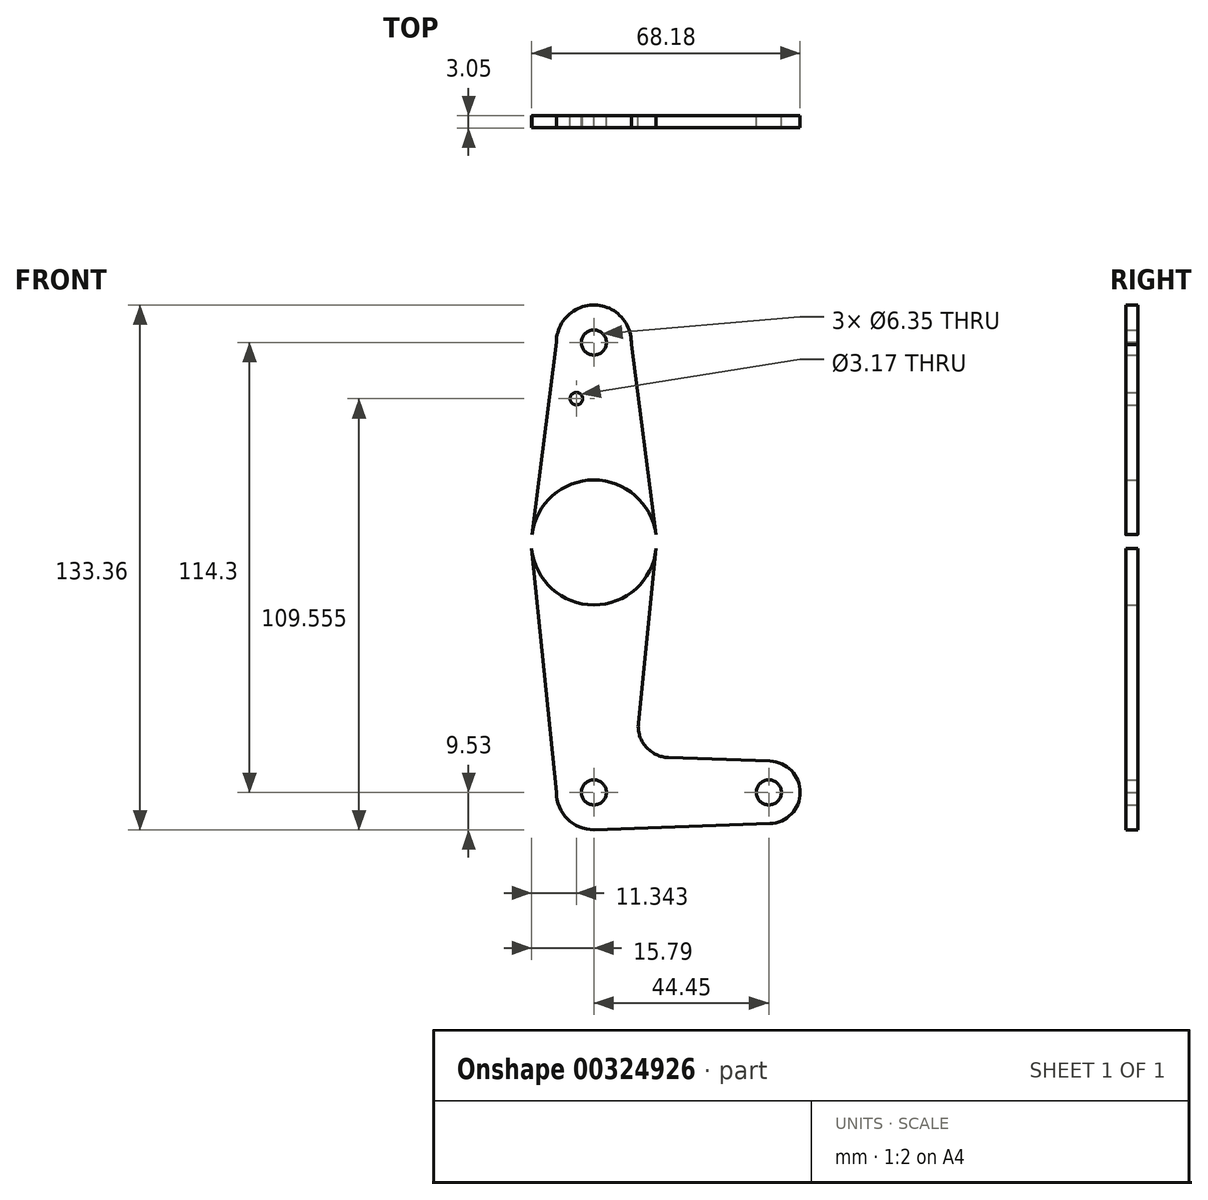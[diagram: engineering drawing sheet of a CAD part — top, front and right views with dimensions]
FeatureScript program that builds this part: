
annotation { "Feature Type Name" : "Feature", "Feature Type Description" : "" }
export const myFeature = defineFeature(function(context is Context, id is Id, definition is map)
    precondition{}
    {
        {
            var Q0;
            Q0=qCreatedBy(makeId("Front.planeOp"),FACE);
            var sketch = newSketch(context, id + "F0", { "sketchPlane" : qUnion([Q0])});
            skLineSegment(sketch, "E0", {"start": v(0, 0) * mm, "end": v(0, 114.3) * mm});
            skLineSegment(sketch, "E1", {"start": v(0, 0) * mm, "end": v(44.45, 0) * mm});
            skCircle(sketch, "E2", {"center": v(0, 114.3) * mm, "radius": 9.52 * mm});
            skCircle(sketch, "E3", {"center": v(44.45, 0) * mm, "radius": 7.94 * mm});
            skCircle(sketch, "E4", {"center": v(0, 0) * mm, "radius": 9.53 * mm});
            skLineSegment(sketch, "E5", {"start": v(0, 0) * mm, "end": v(0, 63.5) * mm});
            skCircle(sketch, "E6", {"center": v(0, 63.5) * mm, "radius": 15.88 * mm});
            skLineSegment(sketch, "E7", {"start": v(-9.52, 114.36) * mm, "end": v(-15.75, 65.5) * mm});
            skLineSegment(sketch, "E8", {"start": v(9.51, 113.81) * mm, "end": v(15.74, 65.53) * mm});
            skLineSegment(sketch, "E9", {"start": v(-9.53, 0) * mm, "end": v(-15.8, 61.9) * mm});
            skLineSegment(sketch, "E10", {"start": v(11.3, 17.6) * mm, "end": v(15.8, 61.9) * mm});
            skLineSegment(sketch, "E11", {"start": v(0, -9.53) * mm, "end": v(44.73, -7.93) * mm});
            skLineSegment(sketch, "E12", {"start": v(18.93, 8.85) * mm, "end": v(44.73, 7.93) * mm});
            skCircle(sketch, "E13", {"center": v(0, 0) * mm, "radius": 3.18 * mm});
            skCircle(sketch, "E14", {"center": v(44.45, 0) * mm, "radius": 3.18 * mm});
            skCircle(sketch, "E15", {"center": v(0, 63.5) * mm, "radius": 3.18 * mm});
            skCircle(sketch, "E16", {"center": v(0, 114.3) * mm, "radius": 3.18 * mm});
            skLineSegment(sketch, "E17", {"start": v(0, 63.5) * mm, "end": v(0, 100.03) * mm});
            skCircle(sketch, "E18", {"center": v(-4.45, 100.03) * mm, "radius": 1.59 * mm});
            skPoint(sketch, "E19.newPointA", {"position": v(0, 9.53) * mm});
            skArc(sketch, "E19.filletArc", {"start": v(11.3, 17.6) * mm, "mid": v(13.22, 11.57) * mm, "end": v(18.93, 8.85) * mm});
            skSolve(sketch);
        }
        {
            var Q0;
            {var subQ0=sQuery(id+"F0.wireOp",EDGE,"E11");var subQ1=sQuery(id+"F0.wireOp",EDGE,"E4");var subQ2=makeQuery(id+"F0.imprint","INTERSECT",VERTEX,{"disambiguationData":[OD(0.0)],"derivedFrom":[subQ1,subQ0]});Q0=makeQuery(id+"F0.imprint","IMPRINT",FACE,{"disambiguationData":[TD([[makeQuery(id+"F0.imprint","IMPRINT",EDGE,{"disambiguationData":[TD([[subQ2,-1.0]])],"derivedFrom":subQ1}),1.0]])]});}
            var Q1;
            {var subQ0=sQuery(id+"F0.wireOp",EDGE,"E8");Q1=makeQuery(id+"F0.imprint","IMPRINT",FACE,{"disambiguationData":[TD([[makeQuery(id+"F0.imprint","IMPRINT",EDGE,{"derivedFrom":subQ0}),-1.0]])]});}
            var Q2;
            {var subQ0=sQuery(id+"F0.wireOp",EDGE,"E3");var subQ1=sQuery(id+"F0.wireOp",EDGE,"E1");var subQ2=makeQuery(id+"F0.imprint","INTERSECT",VERTEX,{"derivedFrom":[subQ1,subQ0]});Q2=makeQuery(id+"F0.imprint","IMPRINT",FACE,{"disambiguationData":[TD([[makeQuery(id+"F0.imprint","IMPRINT",EDGE,{"disambiguationData":[TD([[subQ2,1.0]])],"derivedFrom":subQ1}),-1.0]])]});}
            var Q3;
            Q3=makeQuery(id+"F0.imprint","IMPRINT",FACE,{"disambiguationData":[TD([[makeQuery(id+"F0.imprint","IMPRINT",EDGE,{"derivedFrom":sQuery(id+"F0.wireOp",EDGE,"E16")}),-1.0]])]});
            var Q4;
            Q4=makeQuery(id+"F0.imprint","IMPRINT",FACE,{"disambiguationData":[TD([[makeQuery(id+"F0.imprint","IMPRINT",EDGE,{"derivedFrom":sQuery(id+"F0.wireOp",EDGE,"E14")}),-1.0]])]});
            var Q5;
            {var subQ0=sQuery(id+"F0.wireOp",EDGE,"E9");Q5=makeQuery(id+"F0.imprint","IMPRINT",FACE,{"disambiguationData":[TD([[makeQuery(id+"F0.imprint","IMPRINT",EDGE,{"derivedFrom":subQ0}),-1.0]])]});}
            var Q6;
            {var subQ0=sQuery(id+"F0.wireOp",EDGE,"E7");Q6=makeQuery(id+"F0.imprint","IMPRINT",FACE,{"disambiguationData":[TD([[makeQuery(id+"F0.imprint","IMPRINT",EDGE,{"derivedFrom":subQ0}),1.0]])]});}
            var Q7;
            {var subQ0=sQuery(id+"F0.wireOp",EDGE,"E6");var subQ2=sQuery(id+"F0.wireOp",EDGE,"E5");var subQ3=makeQuery(id+"F0.imprint","INTERSECT",VERTEX,{"derivedFrom":[subQ2,subQ0]});Q7=makeQuery(id+"F0.imprint","IMPRINT",FACE,{"disambiguationData":[TD([[makeQuery(id+"F0.imprint","IMPRINT",EDGE,{"disambiguationData":[TD([[subQ3,-1.0]])],"derivedFrom":subQ2}),-1.0]])]});}
            var Q8;
            {var subQ0=sQuery(id+"F0.wireOp",EDGE,"E6");var subQ5=sQuery(id+"F0.wireOp",EDGE,"E5");var subQ6=makeQuery(id+"F0.imprint","INTERSECT",VERTEX,{"derivedFrom":[subQ5,subQ0]});Q8=makeQuery(id+"F0.imprint","IMPRINT",FACE,{"disambiguationData":[TD([[makeQuery(id+"F0.imprint","IMPRINT",EDGE,{"disambiguationData":[TD([[subQ6,-1.0]])],"derivedFrom":subQ5}),1.0]])]});}
            var Q9;
            {var subQ10=sQuery(id+"F0.wireOp",EDGE,"E10");Q9=makeQuery(id+"F0.imprint","IMPRINT",FACE,{"disambiguationData":[TD([[makeQuery(id+"F0.imprint","IMPRINT",EDGE,{"derivedFrom":subQ10}),1.0]])]});}
            var Q10;
            {var subQ0=sQuery(id+"F0.wireOp",EDGE,"E13");var subQ1=sQuery(id+"F0.wireOp",EDGE,"E1");var subQ2=makeQuery(id+"F0.imprint","INTERSECT",VERTEX,{"derivedFrom":[subQ1,subQ0]});Q10=makeQuery(id+"F0.imprint","IMPRINT",FACE,{"disambiguationData":[TD([[makeQuery(id+"F0.imprint","IMPRINT",EDGE,{"disambiguationData":[TD([[subQ2,-1.0]])],"derivedFrom":subQ1}),1.0]])]});}
            var Q11;
            {var subQ3=sQuery(id+"F0.wireOp",EDGE,"E1");var subQ9=sQuery(id+"F0.wireOp",EDGE,"E13");var subQ10=makeQuery(id+"F0.imprint","INTERSECT",VERTEX,{"derivedFrom":[subQ3,subQ9]});Q11=makeQuery(id+"F0.imprint","IMPRINT",FACE,{"disambiguationData":[TD([[makeQuery(id+"F0.imprint","IMPRINT",EDGE,{"disambiguationData":[TD([[subQ10,-1.0]])],"derivedFrom":subQ3}),-1.0]])]});}
            extrude(context, id + "F1", {"entities" : qUnion([Q0, Q1, Q2, Q3, Q4, Q5, Q6, Q7, Q8, Q9, Q10, Q11]), "depth" : 3.05 * mm});
        }
    });
